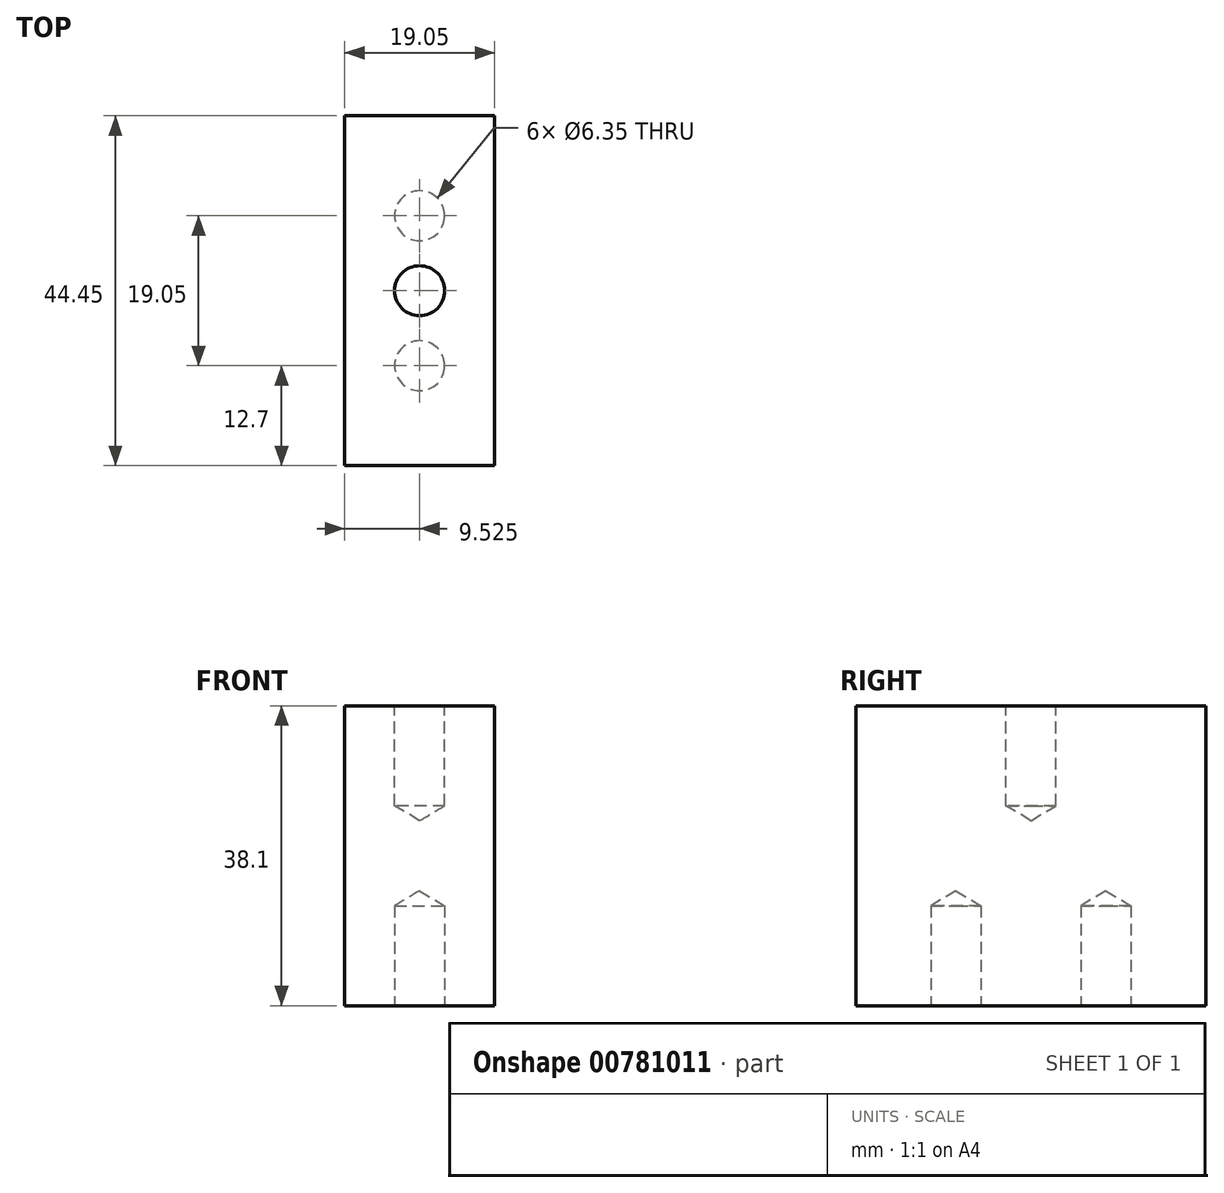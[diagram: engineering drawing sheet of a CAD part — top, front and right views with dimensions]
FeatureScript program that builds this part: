
annotation { "Feature Type Name" : "Feature", "Feature Type Description" : "" }
export const myFeature = defineFeature(function(context is Context, id is Id, definition is map)
    precondition{}
    {
        {
            var Q0;
            Q0=qCreatedBy(makeId("Right.planeOp"),FACE);
            var sketch = newSketch(context, id + "F0", { "sketchPlane" : qUnion([Q0])});
            skLineSegment(sketch, "E0.bottom", {"start": v(0, 0) * mm, "end": v(44.45, 0) * mm});
            skLineSegment(sketch, "E0.top", {"start": v(0, 38.1) * mm, "end": v(44.45, 38.1) * mm});
            skLineSegment(sketch, "E0.left", {"start": v(0, 0) * mm, "end": v(0, 38.1) * mm});
            skLineSegment(sketch, "E0.right", {"start": v(44.45, 0) * mm, "end": v(44.45, 38.1) * mm});
            skSolve(sketch);
        }
        {
            var Q0;
            Q0=makeQuery(id+"F0.imprint","IMPRINT",FACE,{"disambiguationData":[TD([[makeQuery(id+"F0.imprint","IMPRINT",EDGE,{"derivedFrom":sQuery(id+"F0.wireOp",EDGE,"E0.bottom")}),1.0]])]});
            extrude(context, id + "F1", {"entities" : qUnion([Q0]), "depth" : 19.05 * mm, "offsetDistance" : 25.4 * mm});
        }
        {
            var Q0;
            Q0=makeQuery(id+"F1.opExtrude","SWEPT_FACE",FACE,{"disambiguationData":[OSD([sQuery(id+"F0.wireOp",EDGE,"E0.top")])]});
            var sketch = newSketch(context, id + "F2", { "sketchPlane" : qUnion([Q0])});
            skLineSegment(sketch, "E1", {"start": v(0, 22.23) * mm, "end": v(19.05, 22.23) * mm, "construction": true});
            skPoint(sketch, "E2", {"position": v(9.53, 22.23) * mm});
            skSolve(sketch);
        }
        {
            var Q0;
            Q0=sQuery(id+"F2.wireOp",VERTEX,"E2");
            var Q1;
            Q1=makeQuery(id+"F1.opExtrude","SWEPT_BODY",BODY,{"disambiguationData":[OSD([sQuery(id+"F0.wireOp",EDGE,"E0.bottom"),sQuery(id+"F0.wireOp",EDGE,"E0.top"),sQuery(id+"F0.wireOp",EDGE,"E0.left"),sQuery(id+"F0.wireOp",EDGE,"E0.right")])]});
            hole(context, id + "F3", {"style" : HoleStyle.SIMPLE, "endStyle" : HoleEndStyle.BLIND, "holeDiameter" : 6.35 * mm, "majorDiameter" : 6.35 * mm, "holeDepth" : 12.7 * mm, "isTappedThrough" : true, "tappedDepth" : 12.7 * mm, "tapClearance" : 3, "startFromSketch" : true, "locations" : qUnion([Q0]), "scope" : qUnion([Q1])});
        }
        {
            var Q0;
            Q0=makeQuery(id+"F1.opExtrude","SWEPT_FACE",FACE,{"disambiguationData":[OSD([sQuery(id+"F0.wireOp",EDGE,"E0.bottom")])]});
            var sketch = newSketch(context, id + "F4", { "sketchPlane" : qUnion([Q0])});
            skLineSegment(sketch, "E3", {"start": v(9.53, 0) * mm, "end": v(9.53, -44.45) * mm, "construction": true});
            skLineSegment(sketch, "E4", {"start": v(0, -12.7) * mm, "end": v(19.05, -12.7) * mm, "construction": true});
            skLineSegment(sketch, "E5", {"start": v(0, -31.75) * mm, "end": v(19.05, -31.75) * mm, "construction": true});
            skPoint(sketch, "E6", {"position": v(9.53, -12.7) * mm});
            skPoint(sketch, "E7", {"position": v(9.53, -31.75) * mm});
            skSolve(sketch);
        }
        {
            var Q0;
            Q0=sQuery(id+"F4.wireOp",VERTEX,"E6");
            var Q1;
            Q1=sQuery(id+"F4.wireOp",VERTEX,"E7");
            var Q2;
            Q2=makeQuery(id+"F1.opExtrude","SWEPT_BODY",BODY,{"disambiguationData":[OSD([sQuery(id+"F0.wireOp",EDGE,"E0.bottom"),sQuery(id+"F0.wireOp",EDGE,"E0.top"),sQuery(id+"F0.wireOp",EDGE,"E0.left"),sQuery(id+"F0.wireOp",EDGE,"E0.right")])]});
            hole(context, id + "F5", {"style" : HoleStyle.SIMPLE, "endStyle" : HoleEndStyle.BLIND, "holeDiameter" : 6.35 * mm, "majorDiameter" : 6.35 * mm, "holeDepth" : 12.7 * mm, "isTappedThrough" : true, "tappedDepth" : 12.7 * mm, "tapClearance" : 3, "locations" : qUnion([Q0, Q1]), "scope" : qUnion([Q2])});
        }
    });
